# Revit family: Soap_Dish-Grohe-Essentials-40444_Seriesxxx
name_source: partatom
category: Specialty Equipment
revit_build: Autodesk Revit 2014 (Build: 20130308_1515(x64)
units: mm (PartAtom-declared; Revit-internal decimal feet)

## types (2) — shared parameters
Assembly Code = C1030200
Default Elevation = 43"
Description = Essentials Soap Dish With Holder
Height = 2 3/8"
Installation Type = Wall Mounted
Length = 5"
Manufacturer = Grohe
Price = Prices may vary. Please consult Manufacturer Representative for most up-to-date price list.
Product Page URL = https://www.grohe.us
URL = https://www.grohe.us
Width = 2 1/8"

## per-type parameters (varying)
| type | Finish | Material |
| 40444001 | Metal-Grohe-000-Chrome | Metal-Grohe-000-Chrome |
| 40444EN1 | Metal-Grohe-EN0-Brushed Nickel | Metal-Grohe-EN0-Brushed Nickel |

note: column(s) folded — value = type name in every type: Model

## geometry (parser evidence)
native form markers: Sweep x2
no freeform markers — native parametric forms only
